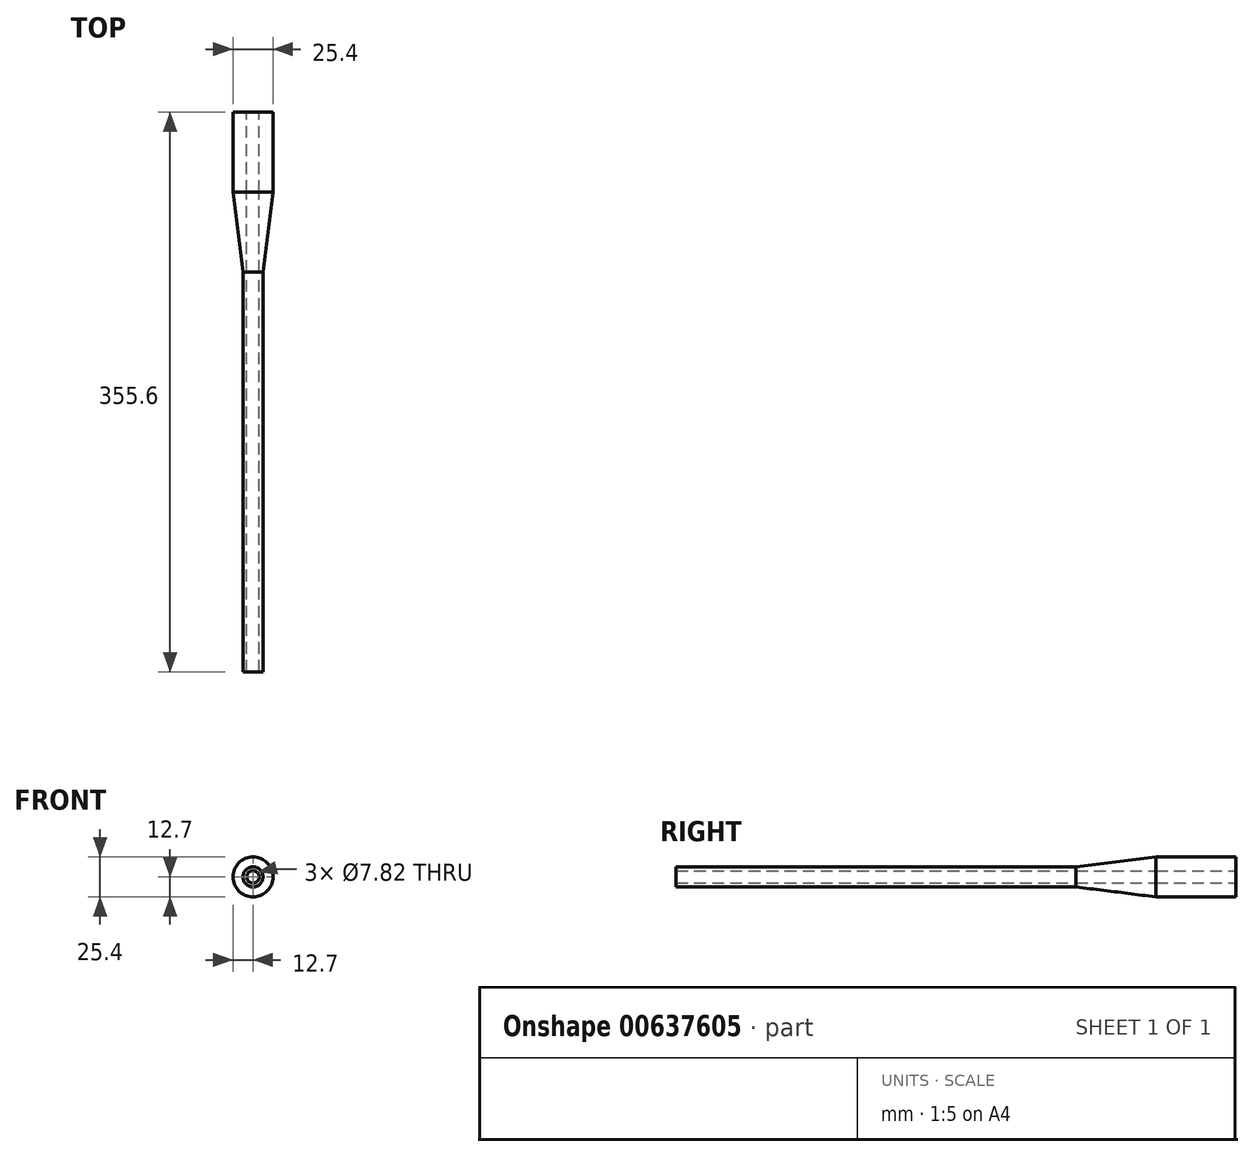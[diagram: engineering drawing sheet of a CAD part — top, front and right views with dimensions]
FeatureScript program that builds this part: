
annotation { "Feature Type Name" : "Feature", "Feature Type Description" : "" }
export const myFeature = defineFeature(function(context is Context, id is Id, definition is map)
    precondition{}
    {
        {
            var Q0;
            Q0=qCreatedBy(makeId("Front.planeOp"),FACE);
            var sketch = newSketch(context, id + "F0", { "sketchPlane" : qUnion([Q0])});
            skCircle(sketch, "E0", {"center": v(0, 0) * mm, "radius": 6.35 * mm});
            skSolve(sketch);
        }
        {
            var Q0;
            Q0=makeQuery(id+"F0.imprint","IMPRINT",FACE,{"disambiguationData":[TD([[makeQuery(id+"F0.imprint","IMPRINT",EDGE,{"derivedFrom":sQuery(id+"F0.wireOp",EDGE,"E0")}),1.0]])]});
            extrude(context, id + "F1", {"entities" : qUnion([Q0]), "depth" : 254 * mm});
        }
        {
            var Q0;
            Q0=qCreatedBy(makeId("Front.planeOp"),FACE);
            cPlane(context, id + "F2", {"entities" : qUnion([Q0]), "cplaneType" : CPlaneType.OFFSET, "offset" : 101.6 * mm, "oppositeDirection" : true, "width" : 152.4 * mm, "height" : 152.4 * mm});
        }
        {
            var Q0;
            Q0=makeQuery(id+"F0.imprint","IMPRINT",FACE,{"disambiguationData":[TD([[makeQuery(id+"F0.imprint","IMPRINT",EDGE,{"derivedFrom":sQuery(id+"F0.wireOp",EDGE,"E0")}),1.0]])]});
            cPlane(context, id + "F3", {"entities" : qUnion([Q0]), "cplaneType" : CPlaneType.OFFSET, "offset" : 50.8 * mm, "oppositeDirection" : true, "width" : 152.4 * mm, "height" : 152.4 * mm});
        }
        {
            var Q0;
            Q0=qCreatedBy(id+"F3.planeOp",FACE);
            var sketch = newSketch(context, id + "F4", { "sketchPlane" : qUnion([Q0])});
            skPoint(sketch, "E1.0", {"position": v(0, 0) * mm});
            skCircle(sketch, "E2", {"center": v(0, 0) * mm, "radius": 12.7 * mm});
            skSolve(sketch);
        }
        {
            var Q0;
            Q0=qCreatedBy(id+"F2.planeOp",FACE);
            var sketch = newSketch(context, id + "F5", { "sketchPlane" : qUnion([Q0])});
            skPoint(sketch, "E3.0", {"position": v(0, 0) * mm});
            skCircle(sketch, "E4", {"center": v(0, 0) * mm, "radius": 12.7 * mm});
            skSolve(sketch);
        }
        {
            var Q0;
            Q0=makeQuery(id+"F5.imprint","IMPRINT",FACE,{"disambiguationData":[TD([[makeQuery(id+"F5.imprint","IMPRINT",EDGE,{"derivedFrom":sQuery(id+"F5.wireOp",EDGE,"E4")}),1.0]])]});
            extrude(context, id + "F6", {"entities" : qUnion([Q0]), "depth" : 50.8 * mm});
        }
        {
            var Q0;
            Q0=makeQuery(id+"F4.imprint","IMPRINT",FACE,{"disambiguationData":[TD([[makeQuery(id+"F4.imprint","IMPRINT",EDGE,{"derivedFrom":sQuery(id+"F4.wireOp",EDGE,"E2")}),1.0]])]});
            var Q1;
            Q1=makeQuery(id+"F0.imprint","IMPRINT",FACE,{"disambiguationData":[TD([[makeQuery(id+"F0.imprint","IMPRINT",EDGE,{"derivedFrom":sQuery(id+"F0.wireOp",EDGE,"E0")}),1.0]])]});
            loft(context, id + "F7", {"sheetProfilesArray" : [{ "sheetProfileEntities" : qUnion([Q0]) }, { "sheetProfileEntities" : qUnion([Q1]) }]});
        }
        {
            var Q0;
            Q0=makeQuery(id+"F5.imprint","IMPRINT",FACE,{"disambiguationData":[TD([[makeQuery(id+"F5.imprint","IMPRINT",EDGE,{"derivedFrom":sQuery(id+"F5.wireOp",EDGE,"E4")}),1.0]])]});
            var sketch = newSketch(context, id + "F8", { "sketchPlane" : qUnion([Q0])});
            skCircle(sketch, "E5", {"center": v(0, 0) * mm, "radius": 3.91 * mm});
            skSolve(sketch);
        }
        {
            var Q0;
            Q0=makeQuery(id+"F8.imprint","IMPRINT",FACE,{"disambiguationData":[TD([[makeQuery(id+"F8.imprint","IMPRINT",EDGE,{"derivedFrom":sQuery(id+"F8.wireOp",EDGE,"E5")}),1.0]])]});
            extrude(context, id + "F9", {"entities" : qUnion([Q0]), "operationType" : NewBodyOperationType.REMOVE, "depth" : 406.4 * mm, "offsetDistance" : 25.4 * mm});
        }
    });
